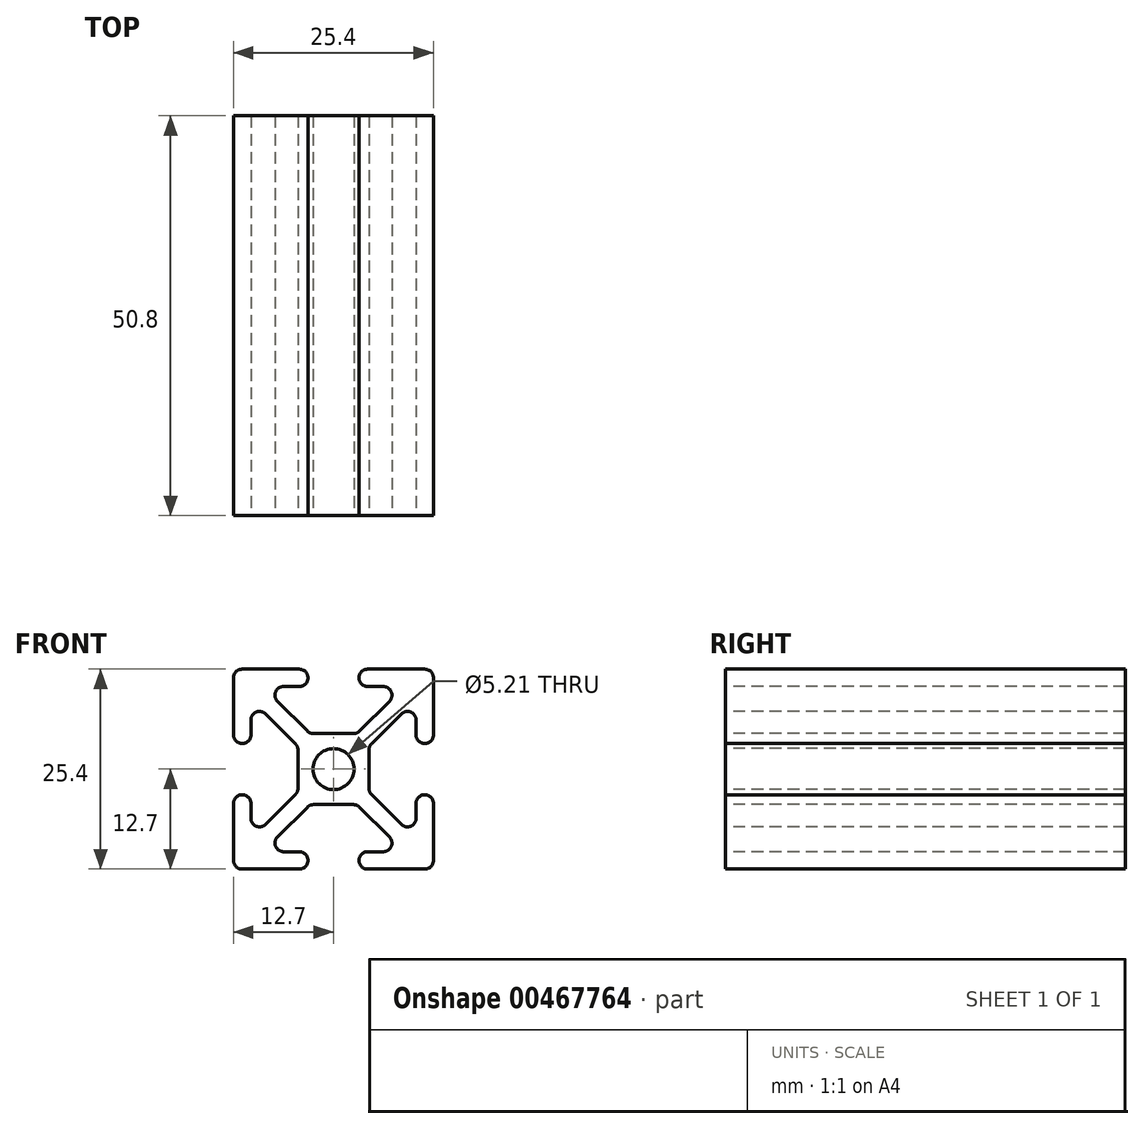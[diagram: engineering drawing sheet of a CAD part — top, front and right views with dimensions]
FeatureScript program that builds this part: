
annotation { "Feature Type Name" : "Feature", "Feature Type Description" : "" }
export const myFeature = defineFeature(function(context is Context, id is Id, definition is map)
    precondition{}
    {
        {
            var Q0;
            Q0=qCreatedBy(makeId("Front.planeOp"),FACE);
            var sketch = newSketch(context, id + "F0", { "sketchPlane" : qUnion([Q0])});
            skLineSegment(sketch, "E0", {"start": v(0, 0) * mm, "end": v(0, 4.5) * mm});
            skLineSegment(sketch, "E1", {"start": v(0, 4.5) * mm, "end": v(-2.54, 4.5) * mm});
            skLineSegment(sketch, "E2", {"start": v(-3.31, 4.83) * mm, "end": v(-7.1, 8.63) * mm});
            skLineSegment(sketch, "E3", {"start": v(-6.34, 10.5) * mm, "end": v(-4.33, 10.5) * mm});
            skLineSegment(sketch, "E4", {"start": v(-3.24, 11.58) * mm, "end": v(-3.24, 11.6) * mm});
            skLineSegment(sketch, "E5", {"start": v(-4.33, 12.7) * mm, "end": v(-11.6, 12.7) * mm});
            skLineSegment(sketch, "E6", {"start": v(-12.7, 11.6) * mm, "end": v(-12.7, 4.34) * mm});
            skLineSegment(sketch, "E7", {"start": v(-11.6, 3.25) * mm, "end": v(-11.58, 3.25) * mm});
            skLineSegment(sketch, "E8", {"start": v(-10.5, 4.34) * mm, "end": v(-10.5, 6.24) * mm});
            skLineSegment(sketch, "E9", {"start": v(-8.63, 7.02) * mm, "end": v(-4.83, 3.22) * mm});
            skLineSegment(sketch, "E10", {"start": v(-4.5, 2.45) * mm, "end": v(-4.5, 0) * mm});
            skLineSegment(sketch, "E11", {"start": v(-4.5, 0) * mm, "end": v(0, 0) * mm});
            skPoint(sketch, "E12.visualSharp", {"position": v(-12.7, 12.7) * mm});
            skArc(sketch, "E12.filletArc", {"start": v(-11.6, 12.7) * mm, "mid": v(-12.38, 12.38) * mm, "end": v(-12.7, 11.6) * mm});
            skPoint(sketch, "E13.visualSharp", {"position": v(-10.5, 3.25) * mm});
            skArc(sketch, "E13.filletArc", {"start": v(-11.58, 3.25) * mm, "mid": v(-10.81, 3.57) * mm, "end": v(-10.5, 4.34) * mm});
            skPoint(sketch, "E14.visualSharp", {"position": v(-12.7, 3.25) * mm});
            skArc(sketch, "E14.filletArc", {"start": v(-12.7, 4.34) * mm, "mid": v(-12.38, 3.57) * mm, "end": v(-11.6, 3.25) * mm});
            skPoint(sketch, "E15.visualSharp", {"position": v(-3.24, 10.5) * mm});
            skArc(sketch, "E15.filletArc", {"start": v(-4.33, 10.5) * mm, "mid": v(-3.56, 10.81) * mm, "end": v(-3.24, 11.58) * mm});
            skPoint(sketch, "E16.visualSharp", {"position": v(-3.24, 12.7) * mm});
            skArc(sketch, "E16.filletArc", {"start": v(-3.24, 11.6) * mm, "mid": v(-3.56, 12.38) * mm, "end": v(-4.33, 12.7) * mm});
            skPoint(sketch, "E17.visualSharp", {"position": v(-8.97, 10.5) * mm});
            skArc(sketch, "E17.filletArc", {"start": v(-6.34, 10.5) * mm, "mid": v(-7.35, 9.82) * mm, "end": v(-7.1, 8.63) * mm});
            skPoint(sketch, "E18.visualSharp", {"position": v(-10.5, 8.88) * mm});
            skArc(sketch, "E18.filletArc", {"start": v(-8.63, 7.02) * mm, "mid": v(-9.82, 7.25) * mm, "end": v(-10.5, 6.24) * mm});
            skPoint(sketch, "E19.visualSharp", {"position": v(-4.5, 2.9) * mm});
            skArc(sketch, "E19.filletArc", {"start": v(-4.5, 2.45) * mm, "mid": v(-4.6, 2.87) * mm, "end": v(-4.83, 3.22) * mm});
            skPoint(sketch, "E20.visualSharp", {"position": v(-3, 4.5) * mm});
            skArc(sketch, "E20.filletArc", {"start": v(-3.31, 4.83) * mm, "mid": v(-2.96, 4.6) * mm, "end": v(-2.54, 4.5) * mm});
            skLineSegment(sketch, "E21.MirrorCS", {"start": v(3.24, 11.58) * mm, "end": v(3.24, 11.6) * mm});
            skArc(sketch, "E22.MirrorCS", {"start": v(12.7, 4.34) * mm, "mid": v(12.38, 3.57) * mm, "end": v(11.6, 3.25) * mm});
            skArc(sketch, "E23.MirrorCS", {"start": v(4.33, 10.5) * mm, "mid": v(3.56, 10.81) * mm, "end": v(3.24, 11.58) * mm});
            skLineSegment(sketch, "E24.MirrorCS", {"start": v(11.6, 3.25) * mm, "end": v(11.58, 3.25) * mm});
            skArc(sketch, "E25.MirrorCS", {"start": v(3.31, 4.83) * mm, "mid": v(2.96, 4.6) * mm, "end": v(2.54, 4.5) * mm});
            skArc(sketch, "E26.MirrorCS", {"start": v(4.5, 2.45) * mm, "mid": v(4.6, 2.87) * mm, "end": v(4.83, 3.22) * mm});
            skArc(sketch, "E27.MirrorCS", {"start": v(11.58, 3.25) * mm, "mid": v(10.81, 3.57) * mm, "end": v(10.5, 4.34) * mm});
            skArc(sketch, "E28.MirrorCS", {"start": v(3.24, 11.6) * mm, "mid": v(3.56, 12.38) * mm, "end": v(4.33, 12.7) * mm});
            skArc(sketch, "E29.MirrorCS", {"start": v(11.6, 12.7) * mm, "mid": v(12.38, 12.38) * mm, "end": v(12.7, 11.6) * mm});
            skArc(sketch, "E30.MirrorCS", {"start": v(8.63, 7.02) * mm, "mid": v(9.82, 7.25) * mm, "end": v(10.5, 6.24) * mm});
            skLineSegment(sketch, "E31.MirrorCS", {"start": v(4.5, 2.45) * mm, "end": v(4.5, 0) * mm});
            skLineSegment(sketch, "E32.MirrorCS", {"start": v(10.5, 4.34) * mm, "end": v(10.5, 6.24) * mm});
            skArc(sketch, "E33.MirrorCS", {"start": v(6.34, 10.5) * mm, "mid": v(7.35, 9.82) * mm, "end": v(7.1, 8.63) * mm});
            skLineSegment(sketch, "E34.MirrorCS", {"start": v(0, 4.5) * mm, "end": v(2.54, 4.5) * mm});
            skLineSegment(sketch, "E35.MirrorCS", {"start": v(6.34, 10.5) * mm, "end": v(4.33, 10.5) * mm});
            skLineSegment(sketch, "E36.MirrorCS", {"start": v(4.33, 12.7) * mm, "end": v(11.6, 12.7) * mm});
            skPoint(sketch, "E37.MirrorP", {"position": v(12.7, 3.25) * mm});
            skLineSegment(sketch, "E38.MirrorCS", {"start": v(4.5, 0) * mm, "end": v(0, 0) * mm});
            skPoint(sketch, "E39.MirrorP", {"position": v(12.7, 12.7) * mm});
            skPoint(sketch, "E40.MirrorP", {"position": v(3, 4.5) * mm});
            skPoint(sketch, "E41.MirrorP", {"position": v(10.5, 3.25) * mm});
            skLineSegment(sketch, "E42.MirrorCS", {"start": v(8.63, 7.02) * mm, "end": v(4.83, 3.22) * mm});
            skPoint(sketch, "E43.MirrorP", {"position": v(3.24, 10.5) * mm});
            skLineSegment(sketch, "E44.MirrorCS", {"start": v(12.7, 11.6) * mm, "end": v(12.7, 4.34) * mm});
            skPoint(sketch, "E45.MirrorP", {"position": v(4.5, 2.9) * mm});
            skPoint(sketch, "E46.MirrorP", {"position": v(10.5, 8.88) * mm});
            skPoint(sketch, "E47.MirrorP", {"position": v(8.97, 10.5) * mm});
            skPoint(sketch, "E48.MirrorP", {"position": v(3.24, 12.7) * mm});
            skLineSegment(sketch, "E49.MirrorCS", {"start": v(3.31, 4.83) * mm, "end": v(7.1, 8.63) * mm});
            skLineSegment(sketch, "E50.MirrorCS", {"start": v(-3.24, -11.58) * mm, "end": v(-3.24, -11.6) * mm});
            skArc(sketch, "E51.MirrorCS", {"start": v(-3.24, -11.6) * mm, "mid": v(-3.56, -12.38) * mm, "end": v(-4.33, -12.7) * mm});
            skArc(sketch, "E52.MirrorCS", {"start": v(-4.33, -10.5) * mm, "mid": v(-3.56, -10.81) * mm, "end": v(-3.24, -11.58) * mm});
            skLineSegment(sketch, "E53.MirrorCS", {"start": v(3.24, -11.58) * mm, "end": v(3.24, -11.6) * mm});
            skArc(sketch, "E54.MirrorCS", {"start": v(3.24, -11.6) * mm, "mid": v(3.56, -12.38) * mm, "end": v(4.33, -12.7) * mm});
            skLineSegment(sketch, "E55.MirrorCS", {"start": v(11.6, -3.25) * mm, "end": v(11.58, -3.25) * mm});
            skLineSegment(sketch, "E56.MirrorCS", {"start": v(0, -4.5) * mm, "end": v(2.54, -4.5) * mm});
            skArc(sketch, "E57.MirrorCS", {"start": v(-3.31, -4.83) * mm, "mid": v(-2.96, -4.6) * mm, "end": v(-2.54, -4.5) * mm});
            skArc(sketch, "E58.MirrorCS", {"start": v(12.7, -4.34) * mm, "mid": v(12.38, -3.57) * mm, "end": v(11.6, -3.25) * mm});
            skArc(sketch, "E59.MirrorCS", {"start": v(3.31, -4.83) * mm, "mid": v(2.96, -4.6) * mm, "end": v(2.54, -4.5) * mm});
            skArc(sketch, "E60.MirrorCS", {"start": v(11.58, -3.25) * mm, "mid": v(10.81, -3.57) * mm, "end": v(10.5, -4.34) * mm});
            skLineSegment(sketch, "E61.MirrorCS", {"start": v(-11.6, -3.25) * mm, "end": v(-11.58, -3.25) * mm});
            skLineSegment(sketch, "E62.MirrorCS", {"start": v(0, -4.5) * mm, "end": v(-2.54, -4.5) * mm});
            skArc(sketch, "E63.MirrorCS", {"start": v(-12.7, -4.34) * mm, "mid": v(-12.38, -3.57) * mm, "end": v(-11.6, -3.25) * mm});
            skArc(sketch, "E64.MirrorCS", {"start": v(-11.58, -3.25) * mm, "mid": v(-10.81, -3.57) * mm, "end": v(-10.5, -4.34) * mm});
            skArc(sketch, "E65.MirrorCS", {"start": v(-4.5, -2.45) * mm, "mid": v(-4.6, -2.87) * mm, "end": v(-4.83, -3.22) * mm});
            skArc(sketch, "E66.MirrorCS", {"start": v(4.5, -2.45) * mm, "mid": v(4.6, -2.87) * mm, "end": v(4.83, -3.22) * mm});
            skLineSegment(sketch, "E67.MirrorCS", {"start": v(10.5, -4.34) * mm, "end": v(10.5, -6.24) * mm});
            skArc(sketch, "E68.MirrorCS", {"start": v(-8.63, -7.02) * mm, "mid": v(-9.82, -7.25) * mm, "end": v(-10.5, -6.24) * mm});
            skArc(sketch, "E69.MirrorCS", {"start": v(11.6, -12.7) * mm, "mid": v(12.38, -12.38) * mm, "end": v(12.7, -11.6) * mm});
            skLineSegment(sketch, "E70.MirrorCS", {"start": v(4.5, -2.45) * mm, "end": v(4.5, 0) * mm});
            skArc(sketch, "E71.MirrorCS", {"start": v(4.33, -10.5) * mm, "mid": v(3.56, -10.81) * mm, "end": v(3.24, -11.58) * mm});
            skArc(sketch, "E72.MirrorCS", {"start": v(-11.6, -12.7) * mm, "mid": v(-12.38, -12.38) * mm, "end": v(-12.7, -11.6) * mm});
            skLineSegment(sketch, "E73.MirrorCS", {"start": v(-4.5, -2.45) * mm, "end": v(-4.5, 0) * mm});
            skLineSegment(sketch, "E74.MirrorCS", {"start": v(-10.5, -4.34) * mm, "end": v(-10.5, -6.24) * mm});
            skLineSegment(sketch, "E75.MirrorCS", {"start": v(-6.34, -10.5) * mm, "end": v(-4.33, -10.5) * mm});
            skArc(sketch, "E76.MirrorCS", {"start": v(6.34, -10.5) * mm, "mid": v(7.35, -9.82) * mm, "end": v(7.1, -8.63) * mm});
            skArc(sketch, "E77.MirrorCS", {"start": v(-6.34, -10.5) * mm, "mid": v(-7.35, -9.82) * mm, "end": v(-7.1, -8.63) * mm});
            skLineSegment(sketch, "E78.MirrorCS", {"start": v(6.34, -10.5) * mm, "end": v(4.33, -10.5) * mm});
            skArc(sketch, "E79.MirrorCS", {"start": v(8.63, -7.02) * mm, "mid": v(9.82, -7.25) * mm, "end": v(10.5, -6.24) * mm});
            skLineSegment(sketch, "E80.MirrorCS", {"start": v(-8.63, -7.02) * mm, "end": v(-4.83, -3.22) * mm});
            skLineSegment(sketch, "E81.MirrorCS", {"start": v(-4.33, -12.7) * mm, "end": v(-11.6, -12.7) * mm});
            skLineSegment(sketch, "E82.MirrorCS", {"start": v(4.33, -12.7) * mm, "end": v(11.6, -12.7) * mm});
            skLineSegment(sketch, "E83.MirrorCS", {"start": v(8.63, -7.02) * mm, "end": v(4.83, -3.22) * mm});
            skPoint(sketch, "E84.MirrorP", {"position": v(-4.5, -2.9) * mm});
            skPoint(sketch, "E85.MirrorP", {"position": v(10.5, -3.25) * mm});
            skLineSegment(sketch, "E86.MirrorCS", {"start": v(12.7, -11.6) * mm, "end": v(12.7, -4.34) * mm});
            skLineSegment(sketch, "E87.MirrorCS", {"start": v(-12.7, -11.6) * mm, "end": v(-12.7, -4.34) * mm});
            skPoint(sketch, "E88.MirrorP", {"position": v(-12.7, -12.7) * mm});
            skPoint(sketch, "E89.MirrorP", {"position": v(-3, -4.5) * mm});
            skPoint(sketch, "E90.MirrorP", {"position": v(4.5, -2.9) * mm});
            skPoint(sketch, "E91.MirrorP", {"position": v(-10.5, -3.25) * mm});
            skPoint(sketch, "E92.MirrorP", {"position": v(8.97, -10.5) * mm});
            skPoint(sketch, "E93.MirrorP", {"position": v(12.7, -3.25) * mm});
            skLineSegment(sketch, "E94.MirrorCS", {"start": v(-3.31, -4.83) * mm, "end": v(-7.1, -8.63) * mm});
            skPoint(sketch, "E95.MirrorP", {"position": v(-12.7, -3.25) * mm});
            skPoint(sketch, "E96.MirrorP", {"position": v(3, -4.5) * mm});
            skLineSegment(sketch, "E97.MirrorCS", {"start": v(0, 0) * mm, "end": v(0, -4.5) * mm});
            skPoint(sketch, "E98.MirrorP", {"position": v(-3.24, -10.5) * mm});
            skPoint(sketch, "E99.MirrorP", {"position": v(-3.24, -12.7) * mm});
            skPoint(sketch, "E100.MirrorP", {"position": v(-8.97, -10.5) * mm});
            skLineSegment(sketch, "E101.MirrorCS", {"start": v(3.31, -4.83) * mm, "end": v(7.1, -8.63) * mm});
            skPoint(sketch, "E102.MirrorP", {"position": v(3.24, -10.5) * mm});
            skPoint(sketch, "E103.MirrorP", {"position": v(10.5, -8.88) * mm});
            skPoint(sketch, "E104.MirrorP", {"position": v(-10.5, -8.88) * mm});
            skPoint(sketch, "E105.MirrorP", {"position": v(12.7, -12.7) * mm});
            skPoint(sketch, "E106.MirrorP", {"position": v(3.24, -12.7) * mm});
            skSolve(sketch);
        }
        {
            var Q0;
            Q0=makeQuery(id+"F0.imprint","IMPRINT",FACE,{"disambiguationData":[TD([[makeQuery(id+"F0.imprint","IMPRINT",EDGE,{"derivedFrom":sQuery(id+"F0.wireOp",EDGE,"E0")}),1.0]])]});
            var Q1;
            Q1=makeQuery(id+"F0.imprint","IMPRINT",FACE,{"disambiguationData":[TD([[makeQuery(id+"F0.imprint","IMPRINT",EDGE,{"derivedFrom":sQuery(id+"F0.wireOp",EDGE,"E0")}),-1.0]])]});
            var Q2;
            Q2=makeQuery(id+"F0.imprint","IMPRINT",FACE,{"disambiguationData":[TD([[makeQuery(id+"F0.imprint","IMPRINT",EDGE,{"derivedFrom":sQuery(id+"F0.wireOp",EDGE,"E53.MirrorCS")}),1.0]])]});
            var Q3;
            Q3=makeQuery(id+"F0.imprint","IMPRINT",FACE,{"disambiguationData":[TD([[makeQuery(id+"F0.imprint","IMPRINT",EDGE,{"derivedFrom":sQuery(id+"F0.wireOp",EDGE,"E11")}),-1.0]])]});
            extrude(context, id + "F1", {"entities" : qUnion([Q0, Q1, Q2, Q3]), "oppositeDirection" : true, "depth" : 50.8 * mm});
        }
        {
            var Q0;
            Q0=makeQuery(id+"F1.opExtrude","CAP_FACE",FACE,{"disambiguationData":[OSD([sQuery(id+"F0.wireOp",EDGE,"E1"),sQuery(id+"F0.wireOp",EDGE,"E2"),sQuery(id+"F0.wireOp",EDGE,"E3"),sQuery(id+"F0.wireOp",EDGE,"E4"),sQuery(id+"F0.wireOp",EDGE,"E5"),sQuery(id+"F0.wireOp",EDGE,"E6"),sQuery(id+"F0.wireOp",EDGE,"E7"),sQuery(id+"F0.wireOp",EDGE,"E8"),sQuery(id+"F0.wireOp",EDGE,"E9"),sQuery(id+"F0.wireOp",EDGE,"E10"),sQuery(id+"F0.wireOp",EDGE,"E12.filletArc"),sQuery(id+"F0.wireOp",EDGE,"E13.filletArc"),sQuery(id+"F0.wireOp",EDGE,"E14.filletArc"),sQuery(id+"F0.wireOp",EDGE,"E15.filletArc"),sQuery(id+"F0.wireOp",EDGE,"E16.filletArc"),sQuery(id+"F0.wireOp",EDGE,"E17.filletArc"),sQuery(id+"F0.wireOp",EDGE,"E18.filletArc"),sQuery(id+"F0.wireOp",EDGE,"E19.filletArc"),sQuery(id+"F0.wireOp",EDGE,"E20.filletArc"),sQuery(id+"F0.wireOp",EDGE,"E21.MirrorCS"),sQuery(id+"F0.wireOp",EDGE,"E22.MirrorCS"),sQuery(id+"F0.wireOp",EDGE,"E23.MirrorCS"),sQuery(id+"F0.wireOp",EDGE,"E24.MirrorCS"),sQuery(id+"F0.wireOp",EDGE,"E25.MirrorCS"),sQuery(id+"F0.wireOp",EDGE,"E26.MirrorCS"),sQuery(id+"F0.wireOp",EDGE,"E27.MirrorCS"),sQuery(id+"F0.wireOp",EDGE,"E28.MirrorCS"),sQuery(id+"F0.wireOp",EDGE,"E29.MirrorCS"),sQuery(id+"F0.wireOp",EDGE,"E30.MirrorCS"),sQuery(id+"F0.wireOp",EDGE,"E31.MirrorCS"),sQuery(id+"F0.wireOp",EDGE,"E32.MirrorCS"),sQuery(id+"F0.wireOp",EDGE,"E33.MirrorCS"),sQuery(id+"F0.wireOp",EDGE,"E34.MirrorCS"),sQuery(id+"F0.wireOp",EDGE,"E35.MirrorCS"),sQuery(id+"F0.wireOp",EDGE,"E36.MirrorCS"),sQuery(id+"F0.wireOp",EDGE,"E42.MirrorCS"),sQuery(id+"F0.wireOp",EDGE,"E44.MirrorCS"),sQuery(id+"F0.wireOp",EDGE,"E49.MirrorCS"),sQuery(id+"F0.wireOp",EDGE,"E50.MirrorCS"),sQuery(id+"F0.wireOp",EDGE,"E51.MirrorCS"),sQuery(id+"F0.wireOp",EDGE,"E52.MirrorCS"),sQuery(id+"F0.wireOp",EDGE,"E53.MirrorCS"),sQuery(id+"F0.wireOp",EDGE,"E54.MirrorCS"),sQuery(id+"F0.wireOp",EDGE,"E55.MirrorCS"),sQuery(id+"F0.wireOp",EDGE,"E56.MirrorCS"),sQuery(id+"F0.wireOp",EDGE,"E57.MirrorCS"),sQuery(id+"F0.wireOp",EDGE,"E58.MirrorCS"),sQuery(id+"F0.wireOp",EDGE,"E59.MirrorCS"),sQuery(id+"F0.wireOp",EDGE,"E60.MirrorCS"),sQuery(id+"F0.wireOp",EDGE,"E61.MirrorCS"),sQuery(id+"F0.wireOp",EDGE,"E62.MirrorCS"),sQuery(id+"F0.wireOp",EDGE,"E63.MirrorCS"),sQuery(id+"F0.wireOp",EDGE,"E64.MirrorCS"),sQuery(id+"F0.wireOp",EDGE,"E65.MirrorCS"),sQuery(id+"F0.wireOp",EDGE,"E66.MirrorCS"),sQuery(id+"F0.wireOp",EDGE,"E67.MirrorCS"),sQuery(id+"F0.wireOp",EDGE,"E68.MirrorCS"),sQuery(id+"F0.wireOp",EDGE,"E69.MirrorCS"),sQuery(id+"F0.wireOp",EDGE,"E70.MirrorCS"),sQuery(id+"F0.wireOp",EDGE,"E71.MirrorCS"),sQuery(id+"F0.wireOp",EDGE,"E72.MirrorCS"),sQuery(id+"F0.wireOp",EDGE,"E73.MirrorCS"),sQuery(id+"F0.wireOp",EDGE,"E74.MirrorCS"),sQuery(id+"F0.wireOp",EDGE,"E75.MirrorCS"),sQuery(id+"F0.wireOp",EDGE,"E76.MirrorCS"),sQuery(id+"F0.wireOp",EDGE,"E77.MirrorCS"),sQuery(id+"F0.wireOp",EDGE,"E78.MirrorCS"),sQuery(id+"F0.wireOp",EDGE,"E79.MirrorCS"),sQuery(id+"F0.wireOp",EDGE,"E80.MirrorCS"),sQuery(id+"F0.wireOp",EDGE,"E81.MirrorCS"),sQuery(id+"F0.wireOp",EDGE,"E82.MirrorCS"),sQuery(id+"F0.wireOp",EDGE,"E83.MirrorCS"),sQuery(id+"F0.wireOp",EDGE,"E86.MirrorCS"),sQuery(id+"F0.wireOp",EDGE,"E87.MirrorCS"),sQuery(id+"F0.wireOp",EDGE,"E94.MirrorCS"),sQuery(id+"F0.wireOp",EDGE,"E101.MirrorCS")])],"isStart":true});
            var sketch = newSketch(context, id + "F2", { "sketchPlane" : qUnion([Q0])});
            skCircle(sketch, "E107", {"center": v(0, 0) * mm, "radius": 2.6 * mm});
            skSolve(sketch);
        }
        {
            var Q0;
            Q0=qSketchRegion(id+"F2",true);
            extrude(context, id + "F3", {"entities" : qUnion([Q0]), "operationType" : NewBodyOperationType.REMOVE, "endBound" : BoundingType.THROUGH_ALL, "oppositeDirection" : true, "depth" : 25.4 * mm});
        }
    });
